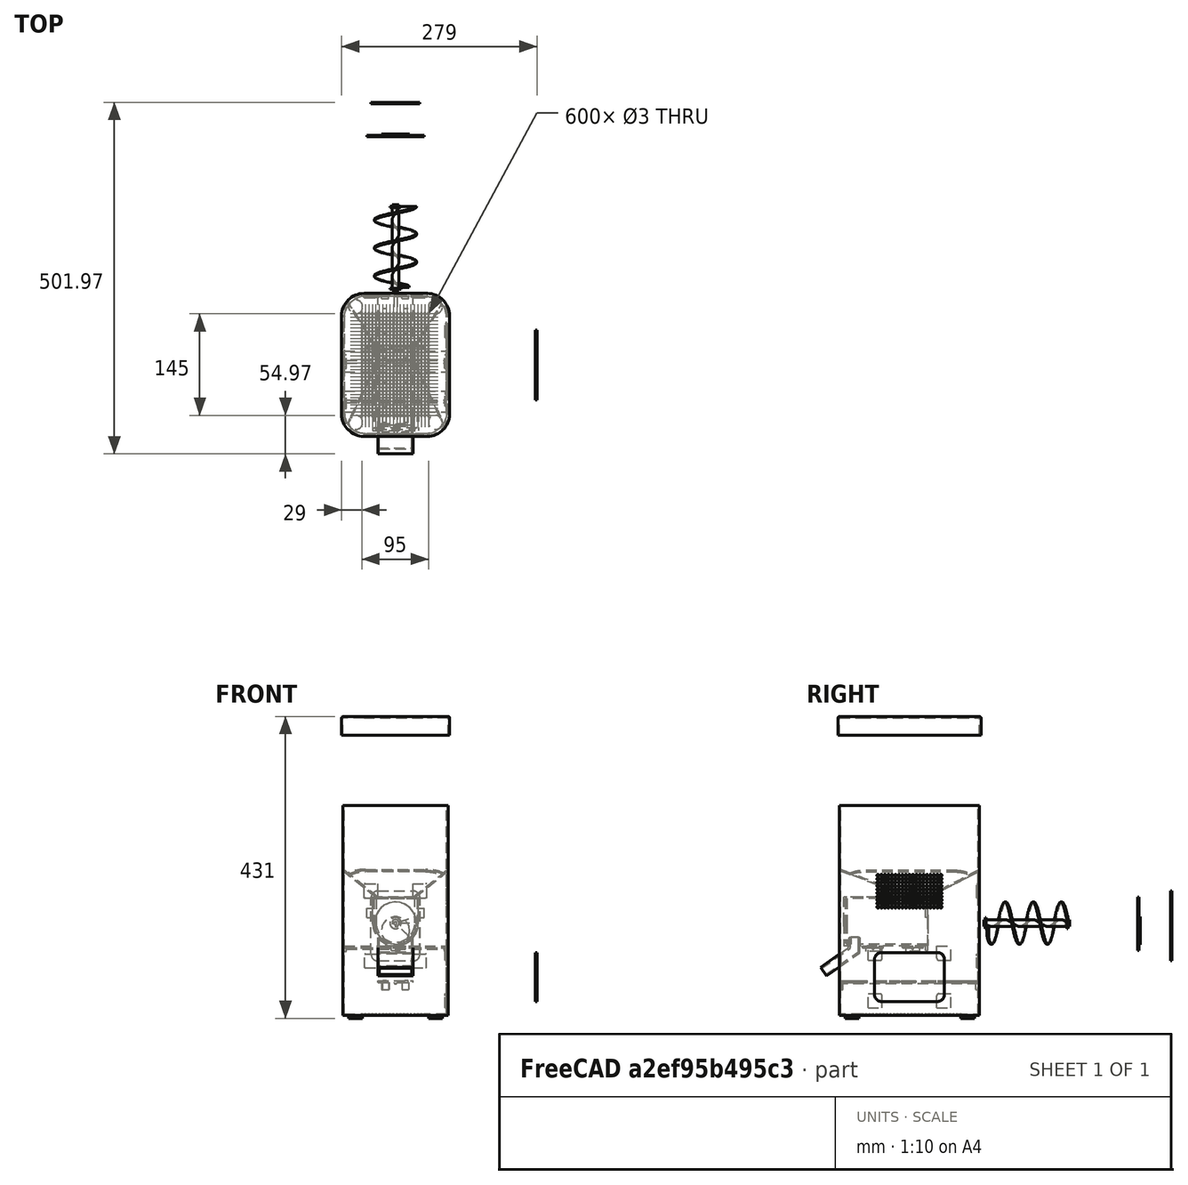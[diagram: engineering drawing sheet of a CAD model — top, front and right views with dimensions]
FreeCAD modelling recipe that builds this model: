
FCSTD DOCUMENT  (FreeCAD 0.18.4R)
Label: alimentador
License: All rights reserved
LicenseURL: http://en.wikipedia.org/wiki/All_rights_reserved
objects: Part::Box×38, Part::Feature×26, Part::Cut×21, Part::MultiFuse×18, Part::Fillet×18, Part::Cylinder×14, Part::FeaturePython×5, Part::Helix×1, Sketcher::SketchObject×1, Part::Sweep×1, Part::Thickness×1, Part::Chamfer×1
note: 145 computed .brp shape members not serialized (recipe doc carries the construction recipe); baked Part::Feature solids carry a one-line shape summary decoded from their .brp

FEATURE [Part::Helix] Helix  label="Hélice"
  Angle = 0
  AttacherType = Attacher::AttachEngine3D
  Height = 115
  LocalCoord = 0
  Pitch = 40
  Radius = 30
  Style = 1
FEATURE [Part::Cylinder] Cylinder  label="Cilindro"
  Angle = 360
  AttacherType = Attacher::AttachEngine3D
  Height = 123
  Placement = pos=(0,0,-2) rot=(0,0,1;0rad)
  Radius = 5
FEATURE [Part::Box] Box  label="Cubo"
  AttacherType = Attacher::AttachEngine3D
  Height = 10
  Length = 50
  Placement = pos=(0,0,-9) rot=(0,0,1;0rad)
  Width = 20
FEATURE [Part::Cylinder] Cylinder001  label="Cilindro001"
  Angle = 340
  AttacherType = Attacher::AttachEngine3D
  Height = 1
  Placement = pos=(0,0,1) rot=(0,0,1;0.331613rad)
  Radius = 8
FEATURE [Part::Cylinder] Cylinder002  label="Cilindro002"
  Angle = 360
  AttacherType = Attacher::AttachEngine3D
  Height = 1
  Placement = pos=(0,0,117.6) rot=(0,0,1;0rad)
  Radius = 8
FEATURE [Part::Box] Box002  label="Cubo002"
  AttacherType = Attacher::AttachEngine3D
  Height = 6
  Length = 3
  Placement = pos=(-1.5,-2.5,-2) rot=(0,0,1;0rad)
  Width = 5
FEATURE [Part::Cylinder] Cylinder003  label="Cilindro003"
  Angle = 360
  AttacherType = Attacher::AttachEngine3D
  Height = 120
  Radius = 32.5
FEATURE [Part::Box] Box003  label="Cubo003"
  AttacherType = Attacher::AttachEngine3D
  Height = 120
  Length = 65
  Placement = pos=(-32.5,0,0) rot=(0,0,1;0rad)
  Width = 37
FEATURE [Part::MultiFuse] Fusion003  label="tolva-externa"
  Refine = true
  Shapes = -> [Cylinder003,Box003]
FEATURE [Part::Cylinder] Cylinder004  label="Cilindro004"
  Angle = 360
  AttacherType = Attacher::AttachEngine3D
  Height = 120
  Radius = 30.5
FEATURE [Part::Box] Box004  label="Cubo004"
  AttacherType = Attacher::AttachEngine3D
  Height = 120
  Length = 61
  Placement = pos=(-30.5,0,0) rot=(0,0,1;0rad)
  Width = 35
FEATURE [Part::MultiFuse] Fusion004  label="tolva-interna"
  Placement = pos=(0,0,-2) rot=(0,0,1;0rad)
  Refine = true
  Shapes = -> [Cylinder004,Box004]
FEATURE [Part::Box] Box005  label="Cubo005"
  AttacherType = Attacher::AttachEngine3D
  Height = 15
  Length = 50
  Placement = pos=(-25,-35,97) rot=(0,0,1;0rad)
  Width = 20
FEATURE [Part::MultiFuse] Fusion005
  Refine = true
  Shapes = -> [Fusion003,Box005]
FEATURE [Part::Cut] Cut003
  Base = -> Fusion005
  Refine = true
  Tool = -> Fusion004
FEATURE [Part::Box] Box006  label="Cubo006"
  AttacherType = Attacher::AttachEngine3D
  Height = 17.5
  Length = 50
  Placement = pos=(-25,35,3) rot=(0,0,1;0rad)
  Width = 12
FEATURE [Part::Cut] Cut004
  Base = -> Cut003
  Refine = true
  Tool = -> Box006
FEATURE [Part::Box] Box007  label="Cubo007"
  AttacherType = Attacher::AttachEngine3D
  Height = 11
  Length = 46
  Placement = pos=(-23,-36,99) rot=(-1,0,0;0.017453rad)
  Width = 25
FEATURE [Part::Cut] Cut005
  Base = -> Cut004
  Refine = true
  Tool = -> Box007
FEATURE [Part::Cylinder] Cylinder005  label="Cilindro005"
  Angle = 360
  AttacherType = Attacher::AttachEngine3D
  Height = 10
  Placement = pos=(0,0,114) rot=(0,0,1;0rad)
  Radius = 5.1
FEATURE [Part::Cut] Cut006  label="Cuerpo-transportador"
  Base = -> Cut005
  Placement = pos=(0,-300,100) rot=(1,0,0;1.5708rad)
  Refine = true
  Tool = -> Cylinder005
FEATURE [Part::Cylinder] Cylinder006  label="Cilindro006"
  Angle = 360
  AttacherType = Attacher::AttachEngine3D
  Height = 2
  Placement = pos=(0,0,-5) rot=(0,0,1;0rad)
  Radius = 32.5
FEATURE [Part::Box] Box008  label="Cubo008"
  AttacherType = Attacher::AttachEngine3D
  Height = 2
  Length = 65
  Placement = pos=(-32.5,-1,-5) rot=(0,0,1;0rad)
  Width = 38
FEATURE [Part::MultiFuse] Fusion006
  Placement = pos=(0,0,3) rot=(0,0,1;0rad)
  Refine = true
  Shapes = -> [Cylinder006,Box008]
FEATURE [Part::Cylinder] Cylinder007  label="Cilindro007"
  Angle = 360
  AttacherType = Attacher::AttachEngine3D
  Height = 10
  Placement = pos=(0,0,-5) rot=(0,0,1;0rad)
  Radius = 5.1
FEATURE [Part::Cylinder] Cylinder008  label="Cilindro008"
  Angle = 360
  AttacherType = Attacher::AttachEngine3D
  Height = 3
  Placement = pos=(0,-11,-4) rot=(0,0,1;0rad)
  Radius = 20
FEATURE [Part::MultiFuse] Fusion007
  Refine = true
  Shapes = -> [Fusion006,Cylinder008]
FEATURE [Part::Cut] Cut007  label="Tapa-transportador"
  Base = -> Fusion007
  Placement = pos=(75,426,132) rot=(1,0,0;1.5708rad)
  Refine = true
  Tool = -> Cylinder007
FEATURE [Sketcher::SketchObject] Sketch
  MapMode = 3
  Placement = pos=(0,0,0) rot=(1,0,0;1.5708rad)
  Support = -> [Helix]
  sketch-geometry (4):
    g0: LineSegment StartX=-0.001296 StartY=1 StartZ=0 EndX=29.9987 EndY=1 EndZ=0
    g1: LineSegment StartX=29.9987 StartY=1 StartZ=0 EndX=29.9987 EndY=-1 EndZ=0
    g2: LineSegment StartX=29.9987 StartY=-1 StartZ=0 EndX=-0.001296 EndY=-1 EndZ=0
    g3: LineSegment StartX=-0.001296 StartY=-1 StartZ=0 EndX=-0.001296 EndY=1 EndZ=0
  constraints (10):
    c: Coincident(g0,g1)
    c: Coincident(g1,g2)
    c: Coincident(g2,g3)
    c: Coincident(g3,g0)
    c: Horizontal(g0)
    c: Horizontal(g2)
    c: Vertical(g1)
    c: DistanceX(g0,g0) = 30
    c: DistanceY(g1,g1) = 2
    c: Symmetric(g0,g2,g-1)
FEATURE [Part::Sweep] Sweep
  Frenet = true
  Sections = -> [Sketch]
  Solid = true
  Spine = -> Helix
  Transition = 1
FEATURE [Part::Cut] Cut
  Base = -> Sweep
  Refine = true
  Tool = -> Box
FEATURE [Part::MultiFuse] Fusion
  Refine = true
  Shapes = -> [Cut,Cylinder002,Cylinder001,Cylinder]
FEATURE [Part::Cut] Cut008  label="Sin-fin"
  Base = -> Fusion
  Placement = pos=(75,627,132) rot=(1,0,0;1.5708rad)
  Refine = true
  Tool = -> Box002
FEATURE [Part::Box] Box009  label="Cubo009"
  AttacherType = Attacher::AttachEngine3D
  Height = 300
  Length = 150
  Width = 200
FEATURE [Part::Fillet] Fillet
  Base = -> Box009
  Edges = 4 edges r=30: [Edge1,Edge3,Edge5,Edge7]
  Placement = pos=(0,300,0) rot=(0,0,1;0rad)
FEATURE [Part::Box] Box010  label="Cubo010"
  AttacherType = Attacher::AttachEngine3D
  Height = 300
  Length = 146
  Width = 196
FEATURE [Part::Fillet] Fillet001
  Base = -> Box010
  Edges = 4 edges r=30: [Edge1,Edge3,Edge5,Edge7]
  Placement = pos=(2,302,2) rot=(0,0,1;0rad)
FEATURE [Part::Cut] Cut009
  Base = -> Fillet
  Refine = true
  Tool = -> Fillet001
FEATURE [Part::Cylinder] Cylinder009  label="Cilindro009"
  Angle = 360
  AttacherType = Attacher::AttachEngine3D
  Height = 10
  Radius = 1.5
FEATURE [Part::FeaturePython] Array  # Draft array (typed FeaturePython)
  Angle = 360
  ArrayType = 0
  Axis = (0,0,1)
  Base = -> Cylinder009
  Center = (0,0,0)
  Fuse = false
  IntervalAxis = (0,0,0)
  IntervalX = (5,0,0)
  IntervalY = (0,5,0)
  IntervalZ = (0,0,1)
  NumberPolar = 1
  NumberX = 20
  NumberY = 30
  NumberZ = 1
  Placement = pos=(27,328,-6) rot=(0,0,1;0rad)
FEATURE [Part::Cut] Cut010
  Base = -> Cut009
  Refine = true
  Tool = -> Array
FEATURE [Part::Cylinder] Cylinder010  label="Cilindro010"
  Angle = 360
  AttacherType = Attacher::AttachEngine3D
  Height = 4
  Radius = 10
FEATURE [Part::FeaturePython] Array001  # Draft array (typed FeaturePython)
  Angle = 360
  ArrayType = 0
  Axis = (0,0,1)
  Base = -> Cylinder010
  Center = (0,0,0)
  Fuse = false
  IntervalAxis = (0,0,0)
  IntervalX = (114,0,0)
  IntervalY = (0,165,0)
  IntervalZ = (0,0,1)
  NumberPolar = 1
  NumberX = 2
  NumberY = 2
  NumberZ = 1
  Placement = pos=(18,318,-4) rot=(0,0,1;0rad)
FEATURE [Part::MultiFuse] Fusion008
  Refine = true
  Shapes = -> [Cut010,Array001]
FEATURE [Part::Box] Box011  label="Cubo011"
  AttacherType = Attacher::AttachEngine3D
  Height = 70
  Length = 50
  Placement = pos=(-23,-410,-30) rot=(0,0,1;0rad)
  Width = 15
FEATURE [Part::Box] Box012  label="Cubo012"
  AttacherType = Attacher::AttachEngine3D
  Height = 70
  Length = 46
  Placement = pos=(-21,-408,-30) rot=(0,0,1;0rad)
  Width = 11
FEATURE [Part::Cut] Cut011
  Base = -> Box011
  Placement = pos=(0,-175.73,-313.58) rot=(-1,0,0;0.959931rad)
  Refine = true
  Tool = -> Box012
FEATURE [Part::Box] Box013  label="Cubo013"
  AttacherType = Attacher::AttachEngine3D
  Height = 30
  Length = 100
  Placement = pos=(-50,-418,33) rot=(0,0,1;0rad)
  Width = 100
FEATURE [Part::Cut] Cut012
  Base = -> Cut011
  Placement = pos=(-2,-17.5,32) rot=(0,0,1;0rad)
  Refine = true
  Tool = -> Box013
FEATURE [Part::Box] Box014  label="Cubo014"
  AttacherType = Attacher::AttachEngine3D
  Height = 30
  Length = 50
  Placement = pos=(-25,-397,36) rot=(0,0,1;0rad)
  Width = 30
FEATURE [Part::MultiFuse] Fusion009
  Refine = true
  Shapes = -> [Cut006,Cut012]
FEATURE [Part::Cut] Cut013
  Base = -> Fusion009
  Refine = true
  Tool = -> Box014
FEATURE [Part::Box] Box015  label="Cubo015"
  AttacherType = Attacher::AttachEngine3D
  Height = 7
  Length = 50
  Placement = pos=(-25,-399,59) rot=(0,0,1;0rad)
  Width = 2
FEATURE [Part::MultiFuse] Fusion010  label="Cuerpo-transportador-con-caida"
  Placement = pos=(75,726,32) rot=(0,0,1;0rad)
  Refine = true
  Shapes = -> [Cut013,Box015]
FEATURE [Part::Box] Box016  label="Cubo016"
  AttacherType = Attacher::AttachEngine3D
  Height = 40
  Length = 50
  Placement = pos=(50,284.15,76.46) rot=(-1,0,0;0.959931rad)
  Width = 15
FEATURE [Part::Cut] Cut014  label="Carcaza-con-agujero-tranportador"
  Base = -> Fusion008
  Refine = true
  Tool = -> Box016
FEATURE [Part::Box] Box017  label="soporte-transportador-1"
  AttacherType = Attacher::AttachEngine3D
  Height = 3
  Length = 146
  Placement = pos=(2,333,96.5) rot=(0,0,1;0rad)
  Width = 30
FEATURE [Part::Box] Box018  label="soporte-transportador-2"
  AttacherType = Attacher::AttachEngine3D
  Height = 3
  Length = 146
  Placement = pos=(2,390,96.5) rot=(0,0,1;0rad)
  Width = 30
FEATURE [Part::Box] Box019  label="Cubo019"
  AttacherType = Attacher::AttachEngine3D
  Height = 100
  Length = 70
  Placement = pos=(0,523,0) rot=(0,0,1;0rad)
  Width = 2
FEATURE [Part::Fillet] Fillet002  label="corte-tapa-lateral"
  Base = -> Box019
  Edges = 4 edges r=10: [Edge2,Edge4,Edge6,Edge8]
  Placement = pos=(40,-25,78) rot=(0,0,1;0rad)
FEATURE [Part::Box] Box020  label="Cubo020"
  AttacherType = Attacher::AttachEngine3D
  Height = 99.85
  Length = 69.85
  Placement = pos=(0,523,0) rot=(0,0,1;0rad)
  Width = 2
FEATURE [Part::Fillet] Fillet003  label="Tapa-lateral"
  Base = -> Box020
  Edges = 4 edges r=10: [Edge2,Edge4,Edge6,Edge8]
  Placement = pos=(40,250,78) rot=(0,0,1;0rad)
FEATURE [Part::Box] Box021  label="Cubo021"
  AttacherType = Attacher::AttachEngine3D
  Height = 20
  Length = 20
  Placement = pos=(31,496,68) rot=(0,0,1;0rad)
  Width = 2
FEATURE [Part::Box] Box022  label="Cubo022"
  AttacherType = Attacher::AttachEngine3D
  Height = 20
  Length = 20
  Placement = pos=(99,496,68) rot=(0,0,1;0rad)
  Width = 2
FEATURE [Part::Box] Box023  label="Cubo023"
  AttacherType = Attacher::AttachEngine3D
  Height = 20
  Length = 20
  Placement = pos=(100,496,168) rot=(0,0,1;0rad)
  Width = 2
FEATURE [Part::Box] Box024  label="Cubo024"
  AttacherType = Attacher::AttachEngine3D
  Height = 20
  Length = 20
  Placement = pos=(30,496,168) rot=(0,0,1;0rad)
  Width = 2
FEATURE [Part::Fillet] Fillet004  label="esquina-tapa-lateral-2"
  Base = -> Box024
  Edges = 1 edges r=3: [Edge8]
FEATURE [Part::Fillet] Fillet005  label="esquina-tapa-lateral-3"
  Base = -> Box023
  Edges = 1 edges r=2: [Edge4]
FEATURE [Part::Fillet] Fillet006  label="esquina-tapa-lateral-1"
  Base = -> Box022
  Edges = 1 edges r=3: [Edge2]
FEATURE [Part::Fillet] Fillet007  label="esquina-tapa-lateral-4"
  Base = -> Box021
  Edges = 1 edges r=3: [Edge6]
FEATURE [Part::Box] Box025  label="Cubo025"
  AttacherType = Attacher::AttachEngine3D
  Height = 70
  Length = 100
  Placement = pos=(0,523,0) rot=(0,0,1;0rad)
  Width = 2
FEATURE [Part::Fillet] Fillet008  label="corte-tapa-trasera"
  Base = -> Box025
  Edges = 4 edges r=10: [Edge2,Edge4,Edge6,Edge8]
  Placement = pos=(673,350,20) rot=(0,0,1;1.5708rad)
FEATURE [Part::Box] Box026  label="Cubo026"
  AttacherType = Attacher::AttachEngine3D
  Height = 69.85
  Length = 99.85
  Placement = pos=(0,523,0) rot=(0,0,1;0rad)
  Width = 2
FEATURE [Part::Fillet] Fillet009  label="Tapa-trasera"
  Base = -> Box026
  Edges = 4 edges r=10: [Edge2,Edge4,Edge6,Edge8]
  Placement = pos=(800,350,20) rot=(0,0,1;1.5708rad)
FEATURE [Part::Cylinder] Cylinder011  label="Cilindro011"
  Angle = 360
  AttacherType = Attacher::AttachEngine3D
  Height = 10
  Radius = 1.5
FEATURE [Part::FeaturePython] Array002  label="agujeros-traseros"  # Draft array (typed FeaturePython)
  Angle = 360
  ArrayType = 0
  Axis = (0,0,1)
  Base = -> Cylinder011
  Center = (0,0,0)
  Fuse = false
  IntervalAxis = (0,0,0)
  IntervalX = (5,0,0)
  IntervalY = (0,5,0)
  IntervalZ = (0,0,1)
  NumberPolar = 1
  NumberX = 10
  NumberY = 19
  NumberZ = 1
  Placement = pos=(144,355,200) rot=(0,1,0;1.5708rad)
FEATURE [Part::Box] Box027  label="Cubo027"
  AttacherType = Attacher::AttachEngine3D
  Height = 20
  Length = 2
  Placement = pos=(146,341,11) rot=(0,0,1;0rad)
  Width = 20
FEATURE [Part::Box] Box028  label="Cubo028"
  AttacherType = Attacher::AttachEngine3D
  Height = 20
  Length = 2
  Placement = pos=(146,439,11) rot=(0,0,1;0rad)
  Width = 20
FEATURE [Part::Box] Box029  label="Cubo029"
  AttacherType = Attacher::AttachEngine3D
  Height = 18
  Length = 2
  Placement = pos=(146,341,79) rot=(0,0,1;0rad)
  Width = 20
FEATURE [Part::Box] Box030  label="Cubo030"
  AttacherType = Attacher::AttachEngine3D
  Height = 20
  Length = 2
  Placement = pos=(146,439,79) rot=(0,0,1;0rad)
  Width = 20
FEATURE [Part::Fillet] Fillet010  label="esquina-tapa-trasera-1"
  Base = -> Box030
  Edges = 1 edges r=3: [Edge9]
FEATURE [Part::Fillet] Fillet011  label="esquina-tapa-trasera-2"
  Base = -> Box029
  Edges = 1 edges r=3: [Edge11]
  Placement = pos=(0,0,-0.2) rot=(0,0,1;0rad)
FEATURE [Part::Fillet] Fillet012  label="esquina-tapa-trasera-3"
  Base = -> Box027
  Edges = 1 edges r=3: [Edge12]
FEATURE [Part::Fillet] Fillet013  label="esquina-tapa-trasera-4"
  Base = -> Box028
  Edges = 1 edges r=3: [Edge10]
FEATURE [Part::Box] Box031  label="soporte-electronica"
  AttacherType = Attacher::AttachEngine3D
  Height = 3
  Length = 50
  Placement = pos=(50,302,47) rot=(0,0,1;0rad)
  Width = 196
FEATURE [Part::Cylinder] Cylinder012  label="soporte-electronica-refuerzo"
  Angle = 360
  AttacherType = Attacher::AttachEngine3D
  Height = 196
  Placement = pos=(75,498,47) rot=(1,0,0;1.5708rad)
  Radius = 2
FEATURE [Part::Box] Box032  label="Cubo032"
  AttacherType = Attacher::AttachEngine3D
  Height = 5
  Length = 5
  Width = 22
FEATURE [Part::FeaturePython] Array003  label="soporte-electronica-agujeros-1"  # Draft array (typed FeaturePython)
  Angle = 360
  ArrayType = 0
  Axis = (0,0,1)
  Base = -> Box032
  Center = (0,0,0)
  Fuse = false
  IntervalAxis = (0,0,0)
  IntervalX = (1,0,0)
  IntervalY = (0,35,0)
  IntervalZ = (0,0,1)
  NumberPolar = 1
  NumberX = 1
  NumberY = 5
  NumberZ = 1
  Placement = pos=(57,318,47) rot=(0,0,1;0rad)
FEATURE [Part::Box] Box033  label="Cubo033"
  AttacherType = Attacher::AttachEngine3D
  Height = 5
  Length = 5
  Width = 22
FEATURE [Part::FeaturePython] Array004  label="soporte-electronica-agujeros-2"  # Draft array (typed FeaturePython)
  Angle = 360
  ArrayType = 0
  Axis = (0,0,1)
  Base = -> Box033
  Center = (0,0,0)
  Fuse = false
  IntervalAxis = (0,0,0)
  IntervalX = (1,0,0)
  IntervalY = (0,35,0)
  IntervalZ = (0,0,1)
  NumberPolar = 1
  NumberX = 1
  NumberY = 5
  NumberZ = 1
  Placement = pos=(88,318,47) rot=(0,0,1;0rad)
FEATURE [Part::Box] Box036  label="Cubo036"
  AttacherType = Attacher::AttachEngine3D
  Height = 25
  Length = 150.2
  Width = 200.2
FEATURE [Part::Fillet] Fillet022
  Base = -> Box036
  Edges = 1 edges r=30: [Edge5]
FEATURE [Part::Fillet] Fillet023
  Base = -> Fillet022
  Edges = 1 edges r=30: [Edge3]
FEATURE [Part::Fillet] Fillet024
  Base = -> Fillet023
  Edges = 1 edges r=30: [Edge18]
FEATURE [Part::Fillet] Fillet025
  Base = -> Fillet024
  Edges = 1 edges r=30: [Edge15]
FEATURE [Part::Thickness] Thickness001  label="Tapa-carcasa"
  Faces = -> Fillet025 [Face10]
  Intersection = false
  Join = 0
  Mode = 0
  Placement = pos=(0,300,400) rot=(0,0,1;0rad)
  SelfIntersection = false
  Value = 2
FEATURE [Part::Feature] Cut021001  label="bandeja-alimentadora"
  Placement = pos=(0,499,-154) rot=(0,0,1;0rad)
  shape: bbox 198.6 x 246.5 x 61.94 mm, 22 faces (baked)
FEATURE [Part::Cut] Cut021002  label="Carcasa-con-agujeros-ventilacion-traseros"
  Base = -> Cut014
  Refine = true
  Tool = -> Array002
FEATURE [Part::Cut] Cut021003  label="Carcasa-con-agujero-tapa-trasero"
  Base = -> Cut021002
  Refine = true
  Tool = -> Fillet008
FEATURE [Part::Cut] Cut021004  label="Carcasa-con-agujero-tapa-lateral"
  Base = -> Cut021003
  Refine = true
  Tool = -> Fillet002
FEATURE [Part::MultiFuse] Fusion011  label="Carcasa-con-esquinas-tapas"
  Refine = true
  Shapes = -> [Cut021004,Fillet013,Fillet012,Fillet011,Fillet010,Fillet007,Fillet005,Fillet004,Fillet006]
FEATURE [Part::MultiFuse] Fusion012  label="Soporte-electronica-con-refuerzo"
  Refine = true
  Shapes = -> [Box031,Cylinder012]
FEATURE [Part::Cut] Cut021005
  Base = -> Fusion012
  Refine = true
  Tool = -> Array003
FEATURE [Part::Cut] Cut021006  label="Soporte-electronica-con-agujeros"
  Base = -> Cut021005
  Refine = true
  Tool = -> Array004
FEATURE [Part::Feature] Box037001  label="Cubo038"
  Placement = pos=(0,338,91.8) rot=(0,0,1;0rad)
  shape: bbox 5 x 20 x 5 mm, 6 faces (baked)
FEATURE [Part::Feature] Box037001001  label="Cubo039"
  Placement = pos=(0,395,91.8) rot=(0,0,1;0rad)
  shape: bbox 5 x 20 x 5 mm, 6 faces (baked)
FEATURE [Part::Feature] Box037001001001  label="Cubo040"
  Placement = pos=(145,395,91.8) rot=(0,0,1;0rad)
  shape: bbox 5 x 20 x 5 mm, 6 faces (baked)
FEATURE [Part::MultiFuse] Fusion013  label="Carcasa-con-soportes-soportes-transportadora"
  Refine = true
  Shapes = -> [Fusion011,Box037001,Box037001001,Box037001001001]
FEATURE [Part::Box] Box037001001002  label="Cubo041"
  AttacherType = Attacher::AttachEngine3D
  Height = 10
  Length = 10
  Placement = pos=(56,300,37) rot=(0,0,1;0rad)
  Width = 5
FEATURE [Part::Feature] Box037001001002001  label="Cubo042"
  Placement = pos=(84,495,37) rot=(0,0,1;0rad)
  shape: bbox 10 x 5 x 10 mm, 6 faces (baked)
FEATURE [Part::Feature] Box037001001002001001  label="Cubo043"
  Placement = pos=(84,300,37) rot=(0,0,1;0rad)
  shape: bbox 10 x 5 x 10 mm, 6 faces (baked)
FEATURE [Part::Feature] Box037001001002001002  label="Cubo044"
  Placement = pos=(55,495,37) rot=(0,0,1;0rad)
  shape: bbox 10 x 5 x 10 mm, 6 faces (baked)
FEATURE [Part::MultiFuse] Fusion014  label="Carcasa-con-soportes-soporte-electronica"
  Refine = true
  Shapes = -> [Fusion013,Box037001001002,Box037001001002001,Box037001001002001001,Box037001001002001002]
FEATURE [Part::Feature] Fusion014001  label="Carcasa-con-soportes-soporte-electronica001"
  Placement = pos=(0,518,0) rot=(0,0,1;0rad)
  shape: bbox 150 x 200 x 304 mm, 931 faces (baked)
FEATURE [Part::Cut] Cut021007  label="Bandeja-alimentadora-con-corte"
  Base = -> Cut021001
  Placement = pos=(0,-518,-77) rot=(0,0,1;0rad)
  Refine = true
  Tool = -> Fusion014001
FEATURE [Part::Feature] Fillet003001  label="Tapa-lateral001"
  shape: bbox 69.85 x 2 x 99.85 mm, 10 faces (baked)
FEATURE [Part::Feature] Fillet009001  label="Tapa-trasera001"
  shape: bbox 2 x 99.85 x 69.85 mm, 10 faces (baked)
FEATURE [Part::Feature] Thickness001001  label="Tapa-carcasa001"
  shape: bbox 159.5 x 209.5 x 27 mm, 27 faces (baked)
FEATURE [Part::Feature] Cut021006001  label="Soporte-electronica-con-agujeros001"
  shape: bbox 50 x 196 x 5 mm, 48 faces (baked)
FEATURE [Part::Feature] Cut021007001  label="Bandeja-alimentadora-con-corte001"
  shape: bbox 191.3 x 235.1 x 55.92 mm, 21 faces (baked)
FEATURE [Part::Box] Box037001001002001003  label="Cubo045"
  AttacherType = Attacher::AttachEngine3D
  Height = 13
  Length = 10
  Placement = pos=(106,423,140) rot=(0,0,1;0rad)
  Width = 3
FEATURE [Part::Feature] Box037001001002001003001  label="Cubo046"
  Placement = pos=(106,426,140) rot=(0,0,1;0rad)
  shape: bbox 10 x 2 x 13 mm, 6 faces (baked)
FEATURE [Part::Feature] Box037001001002001003002  label="Cubo047"
  Placement = pos=(34,423,140) rot=(0,0,1;0rad)
  shape: bbox 10 x 3 x 13 mm, 6 faces (baked)
FEATURE [Part::Feature] Box037001001002001003001001  label="Cubo048"
  Placement = pos=(34,426,140) rot=(0,0,1;0rad)
  shape: bbox 10 x 2 x 13 mm, 6 faces (baked)
FEATURE [Part::Feature] Box037001001002001003001002  label="Cubo049"
  Placement = pos=(69,426,93) rot=(0,0,1;0rad)
  shape: bbox 13 x 2 x 8 mm, 6 faces (baked)
FEATURE [Part::Feature] Box037001001002001003001003  label="Cubo050"
  Placement = pos=(69,423,93) rot=(0,0,1;0rad)
  shape: bbox 13 x 3 x 8 mm, 6 faces (baked)
FEATURE [Part::MultiFuse] Fusion014003  label="Tapa-transportador-completa"
  Placement = pos=(0,300,0) rot=(0,0,1;0rad)
  Refine = true
  Shapes = -> [Cut007,Box037001001002001003001,Box037001001002001003001001,Box037001001002001003001002]
FEATURE [Part::MultiFuse] Fusion014004  label="Cuerpo-transportador-con-caida-y-aletas"
  Refine = true
  Shapes = -> [Fusion010,Box037001001002001003,Box037001001002001003002,Box037001001002001003001003]
FEATURE [Part::Cylinder] Cylinder013  label="Cilindro012"
  Angle = 360
  AttacherType = Attacher::AttachEngine3D
  Height = 140
  Placement = pos=(5,404.5,97) rot=(0,1,0;1.5708rad)
  Radius = 2
FEATURE [Part::Feature] Cylinder013001  label="Cilindro013"
  Placement = pos=(5,348,97) rot=(0,1,0;1.5708rad)
  shape: bbox 140 x 4 x 4 mm, 3 faces (baked)
FEATURE [Part::MultiFuse] Fusion014005  label="soporte-transportador-con-refuerzo-1"
  Refine = true
  Shapes = -> [Box017,Cylinder013001]
FEATURE [Part::MultiFuse] Fusion014006  label="soporte-transportador-con-refuerzo-2"
  Refine = true
  Shapes = -> [Box018,Cylinder013]
FEATURE [Part::Feature] Fusion014003001  label="Tapa-transportador-completa001"
  shape: bbox 82 x 4 x 76 mm, 23 faces (baked)
FEATURE [Part::Feature] Fusion014005001  label="soporte-transportador-con-refuerzo-004"
  shape: bbox 146 x 30 x 4.5 mm, 9 faces (baked)
FEATURE [Part::Feature] Fusion014006001  label="soporte-transportador-con-refuerzo-005"
  shape: bbox 146 x 30 x 4.5 mm, 9 faces (baked)
FEATURE [Part::Feature] Fusion014006002  label="Carcasa-con-soportes-soporte-electronica002"
  shape: bbox 150 x 200 x 304 mm, 931 faces (baked)
FEATURE [Part::Chamfer] Chamfer  label="Cuerpo-transportador-con-caida-chanfle-y-aletas-2"
  Base = -> Fusion014004
  Edges = 1 edges r=3: [Edge78]
FEATURE [Part::Box] Box037001001002001003001004  label="Cubo051"
  AttacherType = Attacher::AttachEngine3D
  Height = 10
  Length = 10
  Placement = pos=(92,506,107) rot=(0,1,0;0.401426rad)
  Width = 10
FEATURE [Part::Cut] Cut021007002  label="Sin-fin-transportador"
  Base = -> Cut008
  Refine = true
  Tool = -> Box037001001002001003001004
FEATURE [Part::Box] Box037001001002001003001005  label="Cubo052"
  AttacherType = Attacher::AttachEngine3D
  Height = 3
  Length = 50
  Placement = pos=(50,312.8,96.5) rot=(1,0,0;0rad)
  Width = 2
FEATURE [Part::Feature] Box037001001002001003001005001  label="Cubo053"
  Placement = pos=(52,314.5,94.5) rot=(-1,0,0;0.418879rad)
  shape: bbox 46 x 6.601 x 6.601 mm, 6 faces (baked)
FEATURE [Part::Cut] Cut021007003
  Base = -> Chamfer
  Refine = true
  Tool = -> Box037001001002001003001005001
FEATURE [Part::MultiFuse] Fusion014006003  label="Cuerpo-transportador-con-caida-chanfle-y-aletas"
  Refine = true
  Shapes = -> [Cut021007003,Box037001001002001003001005]
FEATURE [Part::Feature] Cut021007002001  label="Sin-fin-transportador001"
  shape: bbox 74.19 x 123 x 76.53 mm, 34 faces (baked)
FEATURE [Part::Feature] Fusion014006003001  label="Cuerpo-transportador-con-caida-chanfle-y-aletas001"
  shape: bbox 82 x 153 x 112.2 mm, 51 faces (baked)
